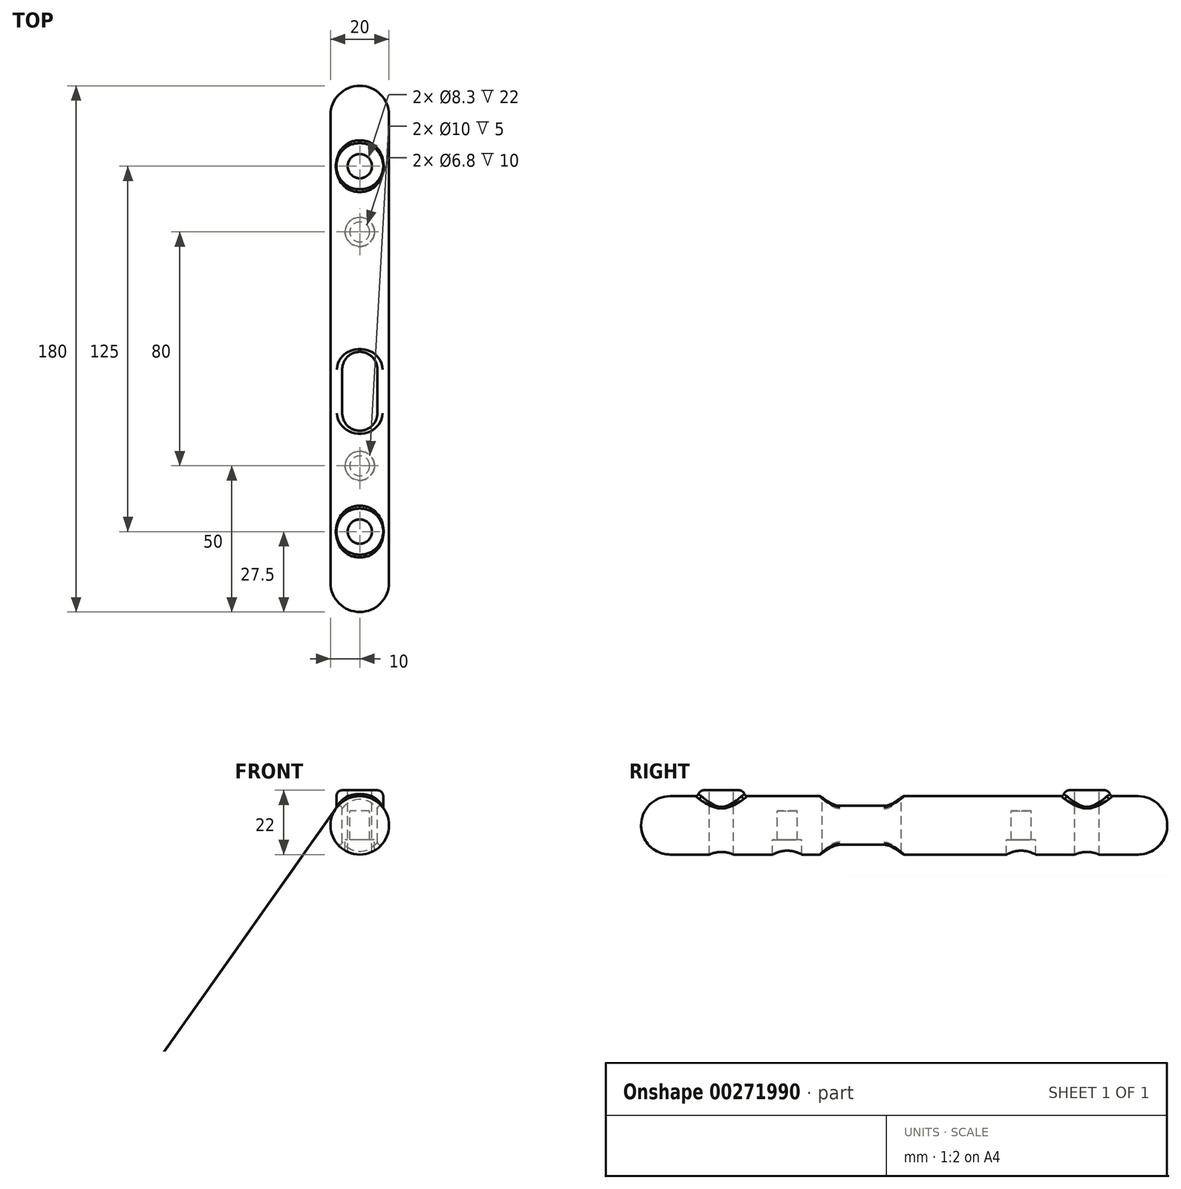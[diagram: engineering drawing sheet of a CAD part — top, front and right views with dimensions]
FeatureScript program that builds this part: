
annotation { "Feature Type Name" : "Feature", "Feature Type Description" : "" }
export const myFeature = defineFeature(function(context is Context, id is Id, definition is map)
    precondition{}
    {
        {
            var Q0;
            Q0=qCreatedBy(makeId("Front.planeOp"),FACE);
            var sketch = newSketch(context, id + "F0", { "sketchPlane" : qUnion([Q0])});
            skCircle(sketch, "E0", {"center": v(0, 0) * mm, "radius": 10 * mm});
            skSolve(sketch);
        }
        {
            var Q0;
            Q0=qCreatedBy(makeId("Right.planeOp"),FACE);
            var sketch = newSketch(context, id + "F1", { "sketchPlane" : qUnion([Q0])});
            skLineSegment(sketch, "E1", {"start": v(0, 0) * mm, "end": v(180, 0) * mm, "construction": true});
            skSolve(sketch);
        }
        {
            var Q0;
            Q0=qCreatedBy(makeId("Top.planeOp"),FACE);
            cPlane(context, id + "F2", {"entities" : qUnion([Q0]), "cplaneType" : CPlaneType.OFFSET, "offset" : 10 * mm, "oppositeDirection" : true, "width" : 150 * mm, "height" : 150 * mm});
        }
        {
            var Q0;
            Q0=qCreatedBy(id+"F2.planeOp",FACE);
            var sketch = newSketch(context, id + "F3", { "sketchPlane" : qUnion([Q0])});
            skLineSegment(sketch, "E2", {"start": v(0, 0) * mm, "end": v(0, 27.5) * mm, "construction": true});
            skLineSegment(sketch, "E3", {"start": v(0, 27.5) * mm, "end": v(0, 50) * mm, "construction": true});
            skLineSegment(sketch, "E4", {"start": v(0, 50) * mm, "end": v(0, 130) * mm, "construction": true});
            skLineSegment(sketch, "E5", {"start": v(0, 130) * mm, "end": v(0, 152.5) * mm, "construction": true});
            skCircle(sketch, "E6", {"center": v(0, 27.5) * mm, "radius": 4.15 * mm});
            skCircle(sketch, "E7", {"center": v(0, 152.5) * mm, "radius": 4.15 * mm});
            skCircle(sketch, "E8", {"center": v(0, 27.5) * mm, "radius": 8 * mm});
            skCircle(sketch, "E9", {"center": v(0, 152.5) * mm, "radius": 8 * mm});
            skCircle(sketch, "E10", {"center": v(0, 50) * mm, "radius": 3.4 * mm});
            skCircle(sketch, "E11", {"center": v(0, 130) * mm, "radius": 3.4 * mm});
            skLineSegment(sketch, "E12", {"start": v(0, 27.5) * mm, "end": v(10, 27.5) * mm, "construction": true});
            skArc(sketch, "E13", {"start": v(10, 22.5) * mm, "mid": v(15, 27.5) * mm, "end": v(10, 32.5) * mm});
            skLineSegment(sketch, "E14", {"start": v(10, 32.5) * mm, "end": v(0, 32.5) * mm});
            skLineSegment(sketch, "E15", {"start": v(10, 22.5) * mm, "end": v(0, 22.5) * mm});
            skLineSegment(sketch, "E16", {"start": v(0, 32.5) * mm, "end": v(0, 31.65) * mm});
            skLineSegment(sketch, "E17", {"start": v(0, 22.5) * mm, "end": v(0, 23.35) * mm});
            skLineSegment(sketch, "E18", {"start": v(0, 0) * mm, "end": v(-30, 0) * mm, "construction": true});
            skLineSegment(sketch, "E19", {"start": v(-30, 0) * mm, "end": v(-30, 90) * mm, "construction": true});
            skLineSegment(sketch, "E20", {"start": v(-30, 90) * mm, "end": v(0, 90) * mm, "construction": true});
            skLineSegment(sketch, "E21.MirrorCS", {"start": v(10, 147.5) * mm, "end": v(0, 147.5) * mm});
            skArc(sketch, "E22.MirrorCS", {"start": v(10, 157.5) * mm, "mid": v(15, 152.5) * mm, "end": v(10, 147.5) * mm});
            skLineSegment(sketch, "E23.MirrorCS", {"start": v(10, 157.5) * mm, "end": v(0, 157.5) * mm});
            skLineSegment(sketch, "E24", {"start": v(0, 147.5) * mm, "end": v(0, 148.35) * mm});
            skLineSegment(sketch, "E25", {"start": v(0, 157.5) * mm, "end": v(0, 156.65) * mm});
            skCircle(sketch, "E26", {"center": v(10, 27.5) * mm, "radius": 2.1 * mm, "construction": true});
            skCircle(sketch, "E27", {"center": v(10, 152.5) * mm, "radius": 2.1 * mm, "construction": true});
            skLineSegment(sketch, "E28", {"start": v(0, 27.5) * mm, "end": v(-25, 27.5) * mm, "construction": true});
            skLineSegment(sketch, "E29", {"start": v(-25, 27.5) * mm, "end": v(-25, 42.5) * mm, "construction": true});
            skCircle(sketch, "E30", {"center": v(-25, 42.5) * mm, "radius": 4 * mm, "construction": true});
            skArc(sketch, "E31", {"start": v(-25, 48.5) * mm, "mid": v(-30.51, 44.86) * mm, "end": v(-29.34, 38.36) * mm});
            skCircle(sketch, "E32.MirrorC", {"center": v(-25, 12.5) * mm, "radius": 4 * mm, "construction": true});
            skArc(sketch, "E33.MirrorC", {"start": v(-25, 6.5) * mm, "mid": v(-30.51, 10.14) * mm, "end": v(-29.34, 16.64) * mm});
            skArc(sketch, "E34", {"start": v(-30, 15.99) * mm, "mid": v(-25, 27.5) * mm, "end": v(-30, 39.01) * mm});
            skPoint(sketch, "E34.first.point", {"position": v(-29.34, 38.36) * mm});
            skPoint(sketch, "E34.second.point", {"position": v(-25, 27.5) * mm});
            skPoint(sketch, "E34.third.point", {"position": v(-29.34, 16.64) * mm});
            skLineSegment(sketch, "E35", {"start": v(0, 0) * mm, "end": v(0, 6.5) * mm, "construction": true});
            skLineSegment(sketch, "E36", {"start": v(0, 6.5) * mm, "end": v(-8, 6.5) * mm, "construction": true});
            skLineSegment(sketch, "E37", {"start": v(-8, 6.5) * mm, "end": v(-8, 48.5) * mm});
            skLineSegment(sketch, "E38", {"start": v(-8, 48.5) * mm, "end": v(-25, 48.5) * mm});
            skLineSegment(sketch, "E39", {"start": v(-8, 6.5) * mm, "end": v(-25, 6.5) * mm});
            skLineSegment(sketch, "E40.0", {"start": v(-5, 6.5) * mm, "end": v(-5, 48.5) * mm});
            skLineSegment(sketch, "E41", {"start": v(-5, 6.5) * mm, "end": v(-8, 6.5) * mm});
            skLineSegment(sketch, "E42", {"start": v(-5, 48.5) * mm, "end": v(-8, 48.5) * mm});
            skSolve(sketch);
        }
        {
            var Q0;
            Q0=qCreatedBy(id+"F2.planeOp",FACE);
            cPlane(context, id + "F4", {"entities" : qUnion([Q0]), "cplaneType" : CPlaneType.OFFSET, "offset" : 20 * mm, "width" : 150 * mm, "height" : 150 * mm});
        }
        {
            var Q0;
            Q0=qCreatedBy(id+"F4.planeOp",FACE);
            var sketch = newSketch(context, id + "F5", { "sketchPlane" : qUnion([Q0])});
            skCircle(sketch, "E43.0", {"center": v(0, 27.5) * mm, "radius": 8 * mm});
            skCircle(sketch, "E44.0", {"center": v(0, 152.5) * mm, "radius": 8 * mm});
            skLineSegment(sketch, "E45", {"start": v(0, 27.5) * mm, "end": v(0, 50) * mm, "construction": true});
            skCircle(sketch, "E46", {"center": v(0, 50) * mm, "radius": 5 * mm, "construction": true});
            skLineSegment(sketch, "E47", {"start": v(0, 50) * mm, "end": v(0, 68) * mm, "construction": true});
            skArc(sketch, "E48", {"start": v(-6, 68) * mm, "mid": v(0, 62) * mm, "end": v(6, 68) * mm});
            skArc(sketch, "E49.MirrorC", {"start": v(-6, 112) * mm, "mid": v(0, 118) * mm, "end": v(6, 112) * mm});
            skLineSegment(sketch, "E50", {"start": v(-6, 68) * mm, "end": v(-6, 83) * mm});
            skLineSegment(sketch, "E51", {"start": v(6, 112) * mm, "end": v(6, 97) * mm});
            skLineSegment(sketch, "E52", {"start": v(0, 68) * mm, "end": v(0, 83) * mm, "construction": true});
            skArc(sketch, "E53", {"start": v(6, 83) * mm, "mid": v(0, 89) * mm, "end": v(-6, 83) * mm});
            skLineSegment(sketch, "E54", {"start": v(-6, 112) * mm, "end": v(6, 112) * mm, "construction": true});
            skLineSegment(sketch, "E55", {"start": v(0, 112) * mm, "end": v(0, 90) * mm, "construction": true});
            skLineSegment(sketch, "E56.0", {"start": v(-6, 90) * mm, "end": v(6, 90) * mm});
            skArc(sketch, "E57.MirrorC", {"start": v(6, 97) * mm, "mid": v(0, 91) * mm, "end": v(-6, 97) * mm});
            skLineSegment(sketch, "E58.trimOffspring", {"start": v(-6, 97) * mm, "end": v(-6, 112) * mm});
            skLineSegment(sketch, "E59.trimOffspring", {"start": v(6, 83) * mm, "end": v(6, 68) * mm});
            skSolve(sketch);
        }
        {
            var Q0;
            Q0=makeQuery(id+"F0.imprint","IMPRINT",FACE,{"disambiguationData":[TD([[makeQuery(id+"F0.imprint","IMPRINT",EDGE,{"derivedFrom":sQuery(id+"F0.wireOp",EDGE,"E0")}),1.0]])]});
            extrude(context, id + "F6", {"entities" : qUnion([Q0]), "oppositeDirection" : true, "depth" : 180 * mm});
        }
        {
            var Q0;
            Q0=makeQuery(id+"F6.opExtrude","CAP_FACE",FACE,{"disambiguationData":[OSD([sQuery(id+"F0.wireOp",EDGE,"E0")])],"isStart":true});
            var Q1;
            Q1=makeQuery(id+"F6.opExtrude","CAP_EDGE",EDGE,{"disambiguationData":[OSD([sQuery(id+"F0.wireOp",EDGE,"E0")])],"isStart":false});
            fillet(context, id + "F7", {"entities" : qUnion([Q0, Q1]), "radius" : 10 * mm, "tangentPropagation" : true, "allowEdgeOverflow" : false});
        }
        {
            var Q0;
            Q0=makeQuery(id+"F5.imprint","IMPRINT",FACE,{"disambiguationData":[TD([[makeQuery(id+"F5.imprint","IMPRINT",EDGE,{"derivedFrom":sQuery(id+"F5.wireOp",EDGE,"E43.0")}),1.0]])]});
            var Q1;
            Q1=makeQuery(id+"F5.imprint","IMPRINT",FACE,{"disambiguationData":[TD([[makeQuery(id+"F5.imprint","IMPRINT",EDGE,{"derivedFrom":sQuery(id+"F5.wireOp",EDGE,"E44.0")}),1.0]])]});
            extrude(context, id + "F8", {"entities" : qUnion([Q0, Q1]), "operationType" : NewBodyOperationType.ADD, "oppositeDirection" : true, "depth" : 10 * mm});
        }
        {
            var Q0;
            Q0=makeQuery(id+"F5.imprint","IMPRINT",FACE,{"disambiguationData":[TD([[makeQuery(id+"F5.imprint","IMPRINT",EDGE,{"derivedFrom":sQuery(id+"F5.wireOp",EDGE,"E43.0")}),1.0]])]});
            var Q1;
            Q1=makeQuery(id+"F5.imprint","IMPRINT",FACE,{"disambiguationData":[TD([[makeQuery(id+"F5.imprint","IMPRINT",EDGE,{"derivedFrom":sQuery(id+"F5.wireOp",EDGE,"E44.0")}),1.0]])]});
            extrude(context, id + "F9", {"entities" : qUnion([Q0, Q1]), "operationType" : NewBodyOperationType.ADD, "depth" : 2 * mm});
        }
        {
            var Q0;
            Q0=makeQuery(id+"F9.opExtrude","CAP_EDGE",EDGE,{"disambiguationData":[OSD([sQuery(id+"F5.wireOp",EDGE,"E43.0")])],"isStart":false});
            var Q1;
            Q1=makeQuery(id+"F9.opExtrude","CAP_FACE",FACE,{"disambiguationData":[OSD([sQuery(id+"F5.wireOp",EDGE,"E44.0")])],"isStart":false});
            fillet(context, id + "F10", {"entities" : qUnion([Q0, Q1]), "radius" : 2 * mm, "tangentPropagation" : true, "allowEdgeOverflow" : false});
        }
        {
            var Q0;
            Q0=qCreatedBy(id+"F4.planeOp",FACE);
            cPlane(context, id + "F11", {"entities" : qUnion([Q0]), "cplaneType" : CPlaneType.OFFSET, "offset" : 2 * mm, "width" : 150 * mm, "height" : 150 * mm});
        }
        {
            var Q0;
            Q0=qCreatedBy(id+"F11.planeOp",FACE);
            var sketch = newSketch(context, id + "F12", { "sketchPlane" : qUnion([Q0])});
            skCircle(sketch, "E60.0", {"center": v(0, 27.5) * mm, "radius": 4.15 * mm});
            skCircle(sketch, "E61.0", {"center": v(0, 152.5) * mm, "radius": 4.15 * mm});
            skSolve(sketch);
        }
        {
            var Q0;
            Q0=makeQuery(id+"F12.imprint","IMPRINT",FACE,{"disambiguationData":[TD([[makeQuery(id+"F12.imprint","IMPRINT",EDGE,{"derivedFrom":sQuery(id+"F12.wireOp",EDGE,"E60.0")}),1.0]])]});
            var Q1;
            Q1=makeQuery(id+"F12.imprint","IMPRINT",FACE,{"disambiguationData":[TD([[makeQuery(id+"F12.imprint","IMPRINT",EDGE,{"derivedFrom":sQuery(id+"F12.wireOp",EDGE,"E61.0")}),1.0]])]});
            extrude(context, id + "F13", {"entities" : qUnion([Q0, Q1]), "operationType" : NewBodyOperationType.REMOVE, "oppositeDirection" : true, "depth" : 25 * mm});
        }
        {
            var Q0;
            Q0=qCreatedBy(id+"F2.planeOp",FACE);
            cPlane(context, id + "F14", {"entities" : qUnion([Q0]), "cplaneType" : CPlaneType.OFFSET, "offset" : 5 * mm, "width" : 150 * mm, "height" : 150 * mm});
        }
        {
            var Q0;
            Q0=qCreatedBy(id+"F14.planeOp",FACE);
            var sketch = newSketch(context, id + "F15", { "sketchPlane" : qUnion([Q0])});
            skLineSegment(sketch, "E62", {"start": v(0, 0) * mm, "end": v(0, 50) * mm, "construction": true});
            skLineSegment(sketch, "E63", {"start": v(0, 50) * mm, "end": v(0, 130) * mm, "construction": true});
            skCircle(sketch, "E64", {"center": v(0, 50) * mm, "radius": 5 * mm});
            skCircle(sketch, "E65", {"center": v(0, 130) * mm, "radius": 5 * mm});
            skSolve(sketch);
        }
        {
            var Q0;
            Q0=qSketchRegion(id+"F15",true);
            extrude(context, id + "F16", {"entities" : qUnion([Q0]), "operationType" : NewBodyOperationType.REMOVE, "oppositeDirection" : true, "depth" : 5 * mm});
        }
        {
            var Q0;
            Q0=qCreatedBy(id+"F14.planeOp",FACE);
            cPlane(context, id + "F17", {"entities" : qUnion([Q0]), "cplaneType" : CPlaneType.OFFSET, "offset" : 10 * mm, "width" : 150 * mm, "height" : 150 * mm});
        }
        {
            var Q0;
            Q0=qCreatedBy(id+"F17.planeOp",FACE);
            var sketch = newSketch(context, id + "F18", { "sketchPlane" : qUnion([Q0])});
            skCircle(sketch, "E66.0", {"center": v(0, 50) * mm, "radius": 3.4 * mm});
            skCircle(sketch, "E67.0", {"center": v(0, 130) * mm, "radius": 3.4 * mm});
            skSolve(sketch);
        }
        {
            var Q0;
            Q0=qSketchRegion(id+"F18",true);
            extrude(context, id + "F19", {"entities" : qUnion([Q0]), "operationType" : NewBodyOperationType.REMOVE, "oppositeDirection" : true, "depth" : 10 * mm});
        }
        {
            var Q0;
            {var subQ0=makeQuery(id+"F8.opExtrude","SWEPT_FACE",FACE,{"disambiguationData":[OSD([sQuery(id+"F5.wireOp",EDGE,"E43.0")])]});var subQ1=makeQuery(id+"F6.opExtrude","SWEPT_FACE",FACE,{"disambiguationData":[OSD([sQuery(id+"F0.wireOp",EDGE,"E0")])]});Q0=makeQuery(id+"F9.boolean.opBoolean","MERGE",EDGE,{"derivedFrom":[makeQuery(id+"F8.boolean.opBoolean","INTERSECT",EDGE,{"disambiguationData":[OD(0.0)],"derivedFrom":[subQ1,subQ0]}),makeQuery(id+"F8.boolean.opBoolean","INTERSECT",EDGE,{"disambiguationData":[OD(1.0)],"derivedFrom":[subQ1,subQ0]})]});}
            var Q1;
            {var subQ0=makeQuery(id+"F8.opExtrude","SWEPT_FACE",FACE,{"disambiguationData":[OSD([sQuery(id+"F5.wireOp",EDGE,"E44.0")])]});var subQ1=makeQuery(id+"F6.opExtrude","SWEPT_FACE",FACE,{"disambiguationData":[OSD([sQuery(id+"F0.wireOp",EDGE,"E0")])]});Q1=makeQuery(id+"F9.boolean.opBoolean","MERGE",EDGE,{"derivedFrom":[makeQuery(id+"F8.boolean.opBoolean","INTERSECT",EDGE,{"disambiguationData":[OD(0.0)],"derivedFrom":[subQ1,subQ0]}),makeQuery(id+"F8.boolean.opBoolean","INTERSECT",EDGE,{"disambiguationData":[OD(1.0)],"derivedFrom":[subQ1,subQ0]})]});}
            fillet(context, id + "F20", {"entities" : qUnion([Q0, Q1]), "radius" : 1 * mm, "tangentPropagation" : true, "allowEdgeOverflow" : false});
        }
        {
            var Q0;
            Q0=makeQuery(id+"F5.imprint","IMPRINT",FACE,{"disambiguationData":[TD([[makeQuery(id+"F5.imprint","IMPRINT",EDGE,{"derivedFrom":sQuery(id+"F5.wireOp",EDGE,"E49.MirrorC")}),-1.0]])]});
            var Q1;
            Q1=makeQuery(id+"F5.imprint","IMPRINT",FACE,{"disambiguationData":[TD([[makeQuery(id+"F5.imprint","IMPRINT",EDGE,{"derivedFrom":sQuery(id+"F5.wireOp",EDGE,"E48")}),1.0]])]});
            extrude(context, id + "F21", {"entities" : qUnion([Q0, Q1]), "operationType" : NewBodyOperationType.REMOVE, "oppositeDirection" : true, "depth" : 20 * mm});
        }
        {
            var Q0;
            Q0=makeQuery(id+"F21.boolean.opBoolean","INTERSECT",EDGE,{"disambiguationData":[OD(1.0)],"derivedFrom":[makeQuery(id+"F6.opExtrude","SWEPT_FACE",FACE,{"disambiguationData":[OSD([sQuery(id+"F0.wireOp",EDGE,"E0")])]}),makeQuery(id+"F21.opExtrude","SWEPT_FACE",FACE,{"disambiguationData":[OSD([sQuery(id+"F5.wireOp",EDGE,"E51")])]})]});
            var Q1;
            Q1=makeQuery(id+"F21.boolean.opBoolean","INTERSECT",EDGE,{"disambiguationData":[OD(1.0)],"derivedFrom":[makeQuery(id+"F6.opExtrude","SWEPT_FACE",FACE,{"disambiguationData":[OSD([sQuery(id+"F0.wireOp",EDGE,"E0")])]}),makeQuery(id+"F21.opExtrude","SWEPT_FACE",FACE,{"disambiguationData":[OSD([sQuery(id+"F5.wireOp",EDGE,"E59.trimOffspring")])]})]});
            var Q2;
            Q2=makeQuery(id+"F21.boolean.opBoolean","INTERSECT",EDGE,{"disambiguationData":[OD(0.0)],"derivedFrom":[makeQuery(id+"F6.opExtrude","SWEPT_FACE",FACE,{"disambiguationData":[OSD([sQuery(id+"F0.wireOp",EDGE,"E0")])]}),makeQuery(id+"F21.opExtrude","SWEPT_FACE",FACE,{"disambiguationData":[OSD([sQuery(id+"F5.wireOp",EDGE,"E49.MirrorC")])]})]});
            var Q3;
            Q3=makeQuery(id+"F21.boolean.opBoolean","INTERSECT",EDGE,{"disambiguationData":[OD(0.0)],"derivedFrom":[makeQuery(id+"F6.opExtrude","SWEPT_FACE",FACE,{"disambiguationData":[OSD([sQuery(id+"F0.wireOp",EDGE,"E0")])]}),makeQuery(id+"F21.opExtrude","SWEPT_FACE",FACE,{"disambiguationData":[OSD([sQuery(id+"F5.wireOp",EDGE,"E53")])]})]});
            fillet(context, id + "F22", {"entities" : qUnion([Q0, Q1, Q2, Q3]), "radius" : 1 * mm, "tangentPropagation" : true, "allowEdgeOverflow" : false});
        }
    });
